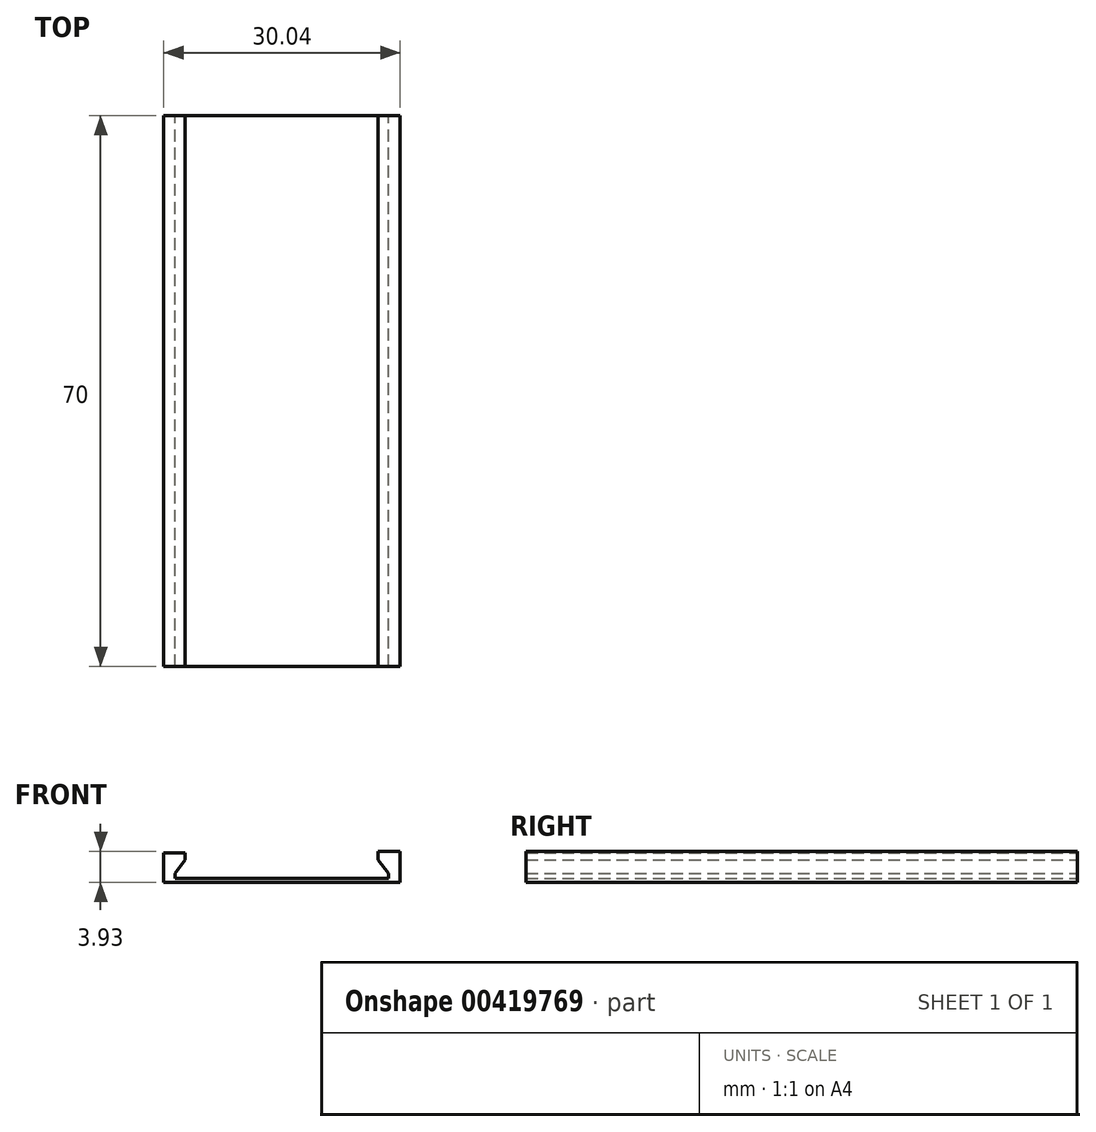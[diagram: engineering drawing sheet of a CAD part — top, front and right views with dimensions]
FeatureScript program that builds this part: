
annotation { "Feature Type Name" : "Feature", "Feature Type Description" : "" }
export const myFeature = defineFeature(function(context is Context, id is Id, definition is map)
    precondition{}
    {
        {
            var Q0;
            Q0=qCreatedBy(makeId("Front.planeOp"),FACE);
            var sketch = newSketch(context, id + "F0", { "sketchPlane" : qUnion([Q0])});
            skLineSegment(sketch, "E0.0", {"start": v(12.24, -2.39) * mm, "end": v(13.55, -4.14) * mm});
            skLineSegment(sketch, "E1.0", {"start": v(-13.56, -4.14) * mm, "end": v(-12.24, -2.39) * mm});
            skLineSegment(sketch, "E2.0", {"start": v(0, -4.77) * mm, "end": v(-13.56, -4.77) * mm});
            skLineSegment(sketch, "E2.1", {"start": v(13.55, -4.77) * mm, "end": v(0, -4.77) * mm});
            skLineSegment(sketch, "E3", {"start": v(13.55, -4.77) * mm, "end": v(13.55, -4.14) * mm});
            skLineSegment(sketch, "E4", {"start": v(-13.56, -4.77) * mm, "end": v(-13.56, -4.14) * mm});
            skLineSegment(sketch, "E5", {"start": v(-12.24, -2.39) * mm, "end": v(-12.24, -1.52) * mm});
            skLineSegment(sketch, "E6", {"start": v(-12.24, -1.52) * mm, "end": v(-14.98, -1.52) * mm});
            skLineSegment(sketch, "E7", {"start": v(-14.98, -1.52) * mm, "end": v(-14.98, -5.27) * mm});
            skLineSegment(sketch, "E8", {"start": v(-14.98, -5.27) * mm, "end": v(15.06, -5.27) * mm});
            skLineSegment(sketch, "E9", {"start": v(15.06, -5.27) * mm, "end": v(15.06, -1.34) * mm});
            skLineSegment(sketch, "E10", {"start": v(15.06, -1.34) * mm, "end": v(12.24, -1.34) * mm});
            skLineSegment(sketch, "E11", {"start": v(12.24, -1.34) * mm, "end": v(12.24, -2.39) * mm});
            skSolve(sketch);
        }
        {
            var Q0;
            Q0=makeQuery(id+"F0.imprint","IMPRINT",FACE,{"disambiguationData":[TD([[makeQuery(id+"F0.imprint","IMPRINT",EDGE,{"derivedFrom":sQuery(id+"F0.wireOp",EDGE,"E0.0")}),1.0]])]});
            extrude(context, id + "F1", {"entities" : qUnion([Q0]), "depth" : 70 * mm});
        }
    });
